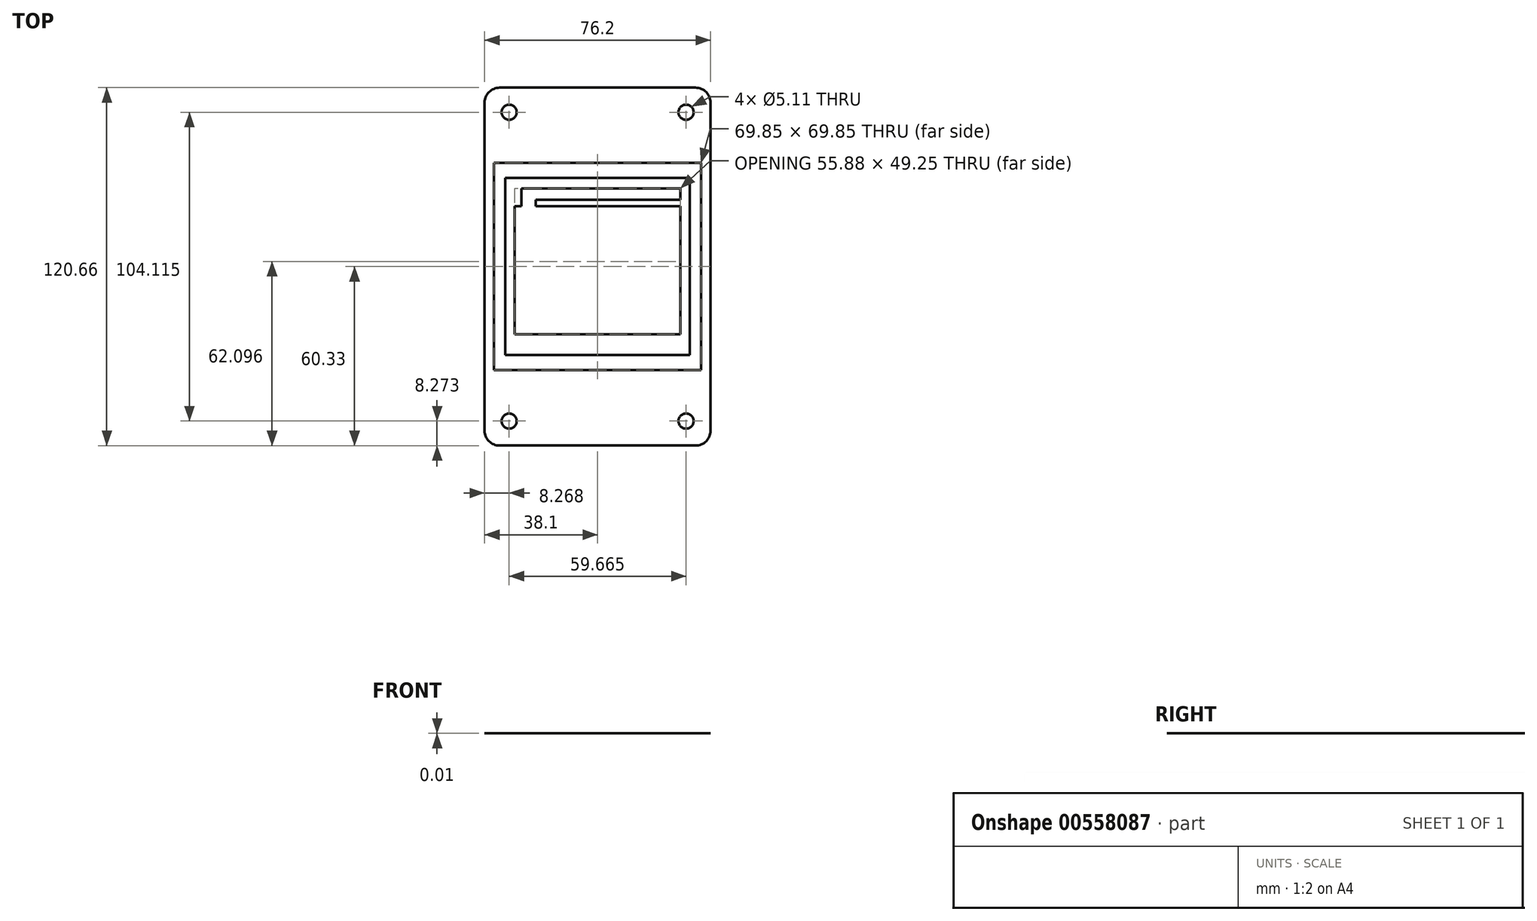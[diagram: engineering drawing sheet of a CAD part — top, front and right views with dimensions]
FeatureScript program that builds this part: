
annotation { "Feature Type Name" : "Feature", "Feature Type Description" : "" }
export const myFeature = defineFeature(function(context is Context, id is Id, definition is map)
    precondition{}
    {
        {
            var Q0;
            Q0=qCreatedBy(makeId("Top.planeOp"),FACE);
            var sketch = newSketch(context, id + "F0", { "sketchPlane" : qUnion([Q0])});
            skLineSegment(sketch, "E0.bottom", {"start": v(-38.1, 60.33) * mm, "end": v(38.1, 60.33) * mm});
            skLineSegment(sketch, "E0.top", {"start": v(-38.1, -60.33) * mm, "end": v(38.1, -60.32) * mm});
            skLineSegment(sketch, "E0.left", {"start": v(-38.1, 60.33) * mm, "end": v(-38.1, -60.33) * mm});
            skLineSegment(sketch, "E0.right", {"start": v(38.1, 60.33) * mm, "end": v(38.1, -60.32) * mm});
            skCircle(sketch, "E1", {"center": v(-29.83, 52.06) * mm, "radius": 2.55 * mm});
            skCircle(sketch, "E2", {"center": v(-29.83, -52.06) * mm, "radius": 2.55 * mm});
            skCircle(sketch, "E3", {"center": v(29.83, -52.06) * mm, "radius": 2.55 * mm});
            skLineSegment(sketch, "E4.bottom", {"start": v(-29.83, 52.06) * mm, "end": v(29.83, 52.06) * mm, "construction": true});
            skLineSegment(sketch, "E4.top", {"start": v(-29.83, -52.06) * mm, "end": v(29.83, -52.06) * mm, "construction": true});
            skLineSegment(sketch, "E4.left", {"start": v(-29.83, 52.06) * mm, "end": v(-29.83, -52.06) * mm, "construction": true});
            skLineSegment(sketch, "E4.right", {"start": v(29.83, 52.06) * mm, "end": v(29.83, -52.06) * mm, "construction": true});
            skPoint(sketch, "E4.middle", {"position": v(0, 0) * mm});
            skCircle(sketch, "E5", {"center": v(29.83, 52.06) * mm, "radius": 2.55 * mm});
            skSolve(sketch);
        }
        {
            var Q0;
            Q0=makeQuery(id+"F0.imprint","IMPRINT",FACE,{"disambiguationData":[TD([[makeQuery(id+"F0.imprint","IMPRINT",EDGE,{"derivedFrom":sQuery(id+"F0.wireOp",EDGE,"E0.bottom")}),-1.0]])]});
            extrude(context, id + "F1", {"entities" : qUnion([Q0]), "depth" : 1 / 101.6 * mm, "offsetDistance" : 25.4 * mm});
        }
        {
            var Q0;
            Q0=makeQuery(id+"F1.opExtrude","CAP_FACE",FACE,{"disambiguationData":[OSD([sQuery(id+"F0.wireOp",EDGE,"E0.bottom"),sQuery(id+"F0.wireOp",EDGE,"E0.top"),sQuery(id+"F0.wireOp",EDGE,"E0.left"),sQuery(id+"F0.wireOp",EDGE,"E0.right"),sQuery(id+"F0.wireOp",EDGE,"E1"),sQuery(id+"F0.wireOp",EDGE,"d460dd98-078a-4822-9f90-65cb2c6fe7cf"),sQuery(id+"F0.wireOp",EDGE,"E2"),sQuery(id+"F0.wireOp",EDGE,"E3")])],"isStart":false});
            var sketch = newSketch(context, id + "F2", { "sketchPlane" : qUnion([Q0])});
            skCircle(sketch, "E6", {"center": v(0, 0) * mm, "radius": 9.53 * mm});
            skLineSegment(sketch, "E7.bottom", {"start": v(-27.94, 20.32) * mm, "end": v(27.94, 20.32) * mm});
            skLineSegment(sketch, "E7.top", {"start": v(-27.94, -22.86) * mm, "end": v(27.94, -22.86) * mm});
            skLineSegment(sketch, "E7.left", {"start": v(-27.94, 20.32) * mm, "end": v(-27.94, -22.86) * mm});
            skLineSegment(sketch, "E7.right", {"start": v(27.94, 20.32) * mm, "end": v(27.94, -22.86) * mm});
            skSolve(sketch);
        }
        {
            var Q0;
            Q0=makeQuery(id+"F2.imprint","IMPRINT",FACE,{"disambiguationData":[TD([[makeQuery(id+"F2.imprint","IMPRINT",EDGE,{"derivedFrom":sQuery(id+"F2.wireOp",EDGE,"E6")}),1.0]])]});
            extrude(context, id + "F3", {"entities" : qUnion([Q0]), "operationType" : NewBodyOperationType.REMOVE, "oppositeDirection" : true, "depth" : 1 / 101.6 * mm, "offsetDistance" : 25.4 * mm});
        }
        {
            var Q0;
            Q0=makeQuery(id+"F2.imprint","IMPRINT",FACE,{"disambiguationData":[TD([[makeQuery(id+"F2.imprint","IMPRINT",EDGE,{"derivedFrom":sQuery(id+"F2.wireOp",EDGE,"E6")}),-1.0]])]});
            extrude(context, id + "F4", {"entities" : qUnion([Q0]), "operationType" : NewBodyOperationType.REMOVE, "oppositeDirection" : true, "depth" : 5 * mm, "offsetDistance" : 25.4 * mm});
        }
        {
            var Q0;
            Q0=makeQuery(id+"F1.opExtrude","SWEPT_EDGE",EDGE,{"disambiguationData":[OSD([sQuery(id+"F0.wireOp",EDGE,"E0.top"),sQuery(id+"F0.wireOp",EDGE,"E0.right")])]});
            var Q1;
            Q1=makeQuery(id+"F1.opExtrude","SWEPT_EDGE",EDGE,{"disambiguationData":[OSD([sQuery(id+"F0.wireOp",EDGE,"E0.bottom"),sQuery(id+"F0.wireOp",EDGE,"E0.right")])]});
            var Q2;
            Q2=makeQuery(id+"F1.opExtrude","SWEPT_EDGE",EDGE,{"disambiguationData":[OSD([sQuery(id+"F0.wireOp",EDGE,"E0.bottom"),sQuery(id+"F0.wireOp",EDGE,"E0.left")])]});
            var Q3;
            Q3=makeQuery(id+"F1.opExtrude","SWEPT_EDGE",EDGE,{"disambiguationData":[OSD([sQuery(id+"F0.wireOp",EDGE,"E0.top"),sQuery(id+"F0.wireOp",EDGE,"E0.left")])]});
            fillet(context, id + "F5", {"entities" : qUnion([Q0, Q1, Q2, Q3]), "radius" : 5.08 * mm, "tangentPropagation" : true, "allowEdgeOverflow" : false});
        }
        {
            var Q0;
            Q0=makeQuery(id+"F1.opExtrude","CAP_FACE",FACE,{"disambiguationData":[OSD([sQuery(id+"F0.wireOp",EDGE,"E0.bottom"),sQuery(id+"F0.wireOp",EDGE,"E0.top"),sQuery(id+"F0.wireOp",EDGE,"E0.left"),sQuery(id+"F0.wireOp",EDGE,"E0.right"),sQuery(id+"F0.wireOp",EDGE,"E1"),sQuery(id+"F0.wireOp",EDGE,"d460dd98-078a-4822-9f90-65cb2c6fe7cf"),sQuery(id+"F0.wireOp",EDGE,"E2"),sQuery(id+"F0.wireOp",EDGE,"E3")])],"isStart":false});
            var sketch = newSketch(context, id + "F6", { "sketchPlane" : qUnion([Q0])});
            skLineSegment(sketch, "E8.bottom", {"start": v(34.93, -34.92) * mm, "end": v(-34.93, -34.93) * mm});
            skLineSegment(sketch, "E8.top", {"start": v(34.92, 34.93) * mm, "end": v(-34.93, 34.92) * mm});
            skLineSegment(sketch, "E8.left", {"start": v(34.93, -34.92) * mm, "end": v(34.92, 34.93) * mm});
            skLineSegment(sketch, "E8.right", {"start": v(-34.93, -34.93) * mm, "end": v(-34.93, 34.92) * mm});
            skLineSegment(sketch, "E9.bottom", {"start": v(31.12, -29.85) * mm, "end": v(-31.12, -29.85) * mm});
            skLineSegment(sketch, "E9.top", {"start": v(31.12, 29.85) * mm, "end": v(-31.12, 29.85) * mm});
            skLineSegment(sketch, "E9.left", {"start": v(31.12, -29.85) * mm, "end": v(31.12, 29.85) * mm});
            skLineSegment(sketch, "E9.right", {"start": v(-31.12, -29.85) * mm, "end": v(-31.12, 29.85) * mm});
            skSolve(sketch);
        }
        {
            var Q0;
            Q0=makeQuery(id+"F6.imprint","IMPRINT",FACE,{"disambiguationData":[TD([[makeQuery(id+"F6.imprint","IMPRINT",EDGE,{"derivedFrom":sQuery(id+"F6.wireOp",EDGE,"E8.bottom")}),-1.0]])]});
            extrude(context, id + "F7", {"entities" : qUnion([Q0]), "operationType" : NewBodyOperationType.REMOVE, "oppositeDirection" : true, "depth" : 0.06 * 17.78 * mm, "offsetDistance" : 25.4 * mm});
        }
        {
            var Q0;
            Q0=makeQuery(id+"F7.boolean.opBoolean","SPLIT",FACE,{"disambiguationData":[TD([makeQuery(id+"F4.boolean.opBoolean","COPY",FACE,{"derivedFrom":makeQuery(id+"F4.opExtrude","SWEPT_FACE",FACE,{"disambiguationData":[OSD([sQuery(id+"F2.wireOp",EDGE,"E7.bottom")])]})})])],"derivedFrom":makeQuery(id+"F1.opExtrude","CAP_FACE",FACE,{"disambiguationData":[OSD([sQuery(id+"F0.wireOp",EDGE,"E0.bottom"),sQuery(id+"F0.wireOp",EDGE,"E0.top"),sQuery(id+"F0.wireOp",EDGE,"E0.left"),sQuery(id+"F0.wireOp",EDGE,"E0.right"),sQuery(id+"F0.wireOp",EDGE,"E1"),sQuery(id+"F0.wireOp",EDGE,"d460dd98-078a-4822-9f90-65cb2c6fe7cf"),sQuery(id+"F0.wireOp",EDGE,"E2"),sQuery(id+"F0.wireOp",EDGE,"E3")])],"isStart":false})});
            var sketch = newSketch(context, id + "F8", { "sketchPlane" : qUnion([Q0])});
            skLineSegment(sketch, "E10", {"start": v(-20.9, 20.32) * mm, "end": v(-20.9, 22.5) * mm});
            skLineSegment(sketch, "E11", {"start": v(-20.9, 22.5) * mm, "end": v(27.94, 22.5) * mm});
            skLineSegment(sketch, "E12", {"start": v(27.94, 22.5) * mm, "end": v(27.94, 26.4) * mm});
            skLineSegment(sketch, "E13", {"start": v(27.94, 26.4) * mm, "end": v(-25.7, 26.4) * mm});
            skLineSegment(sketch, "E14", {"start": v(-25.7, 26.4) * mm, "end": v(-25.7, 20.32) * mm});
            skSolve(sketch);
        }
        {
            var Q0;
            {var subQ0=sQuery(id+"F8.wireOp",EDGE,"E10");Q0=makeQuery(id+"F8.imprint","IMPRINT",FACE,{"disambiguationData":[TD([[makeQuery(id+"F8.imprint","IMPRINT",EDGE,{"derivedFrom":subQ0}),1.0]])]});}
            extrude(context, id + "F9", {"entities" : qUnion([Q0]), "operationType" : NewBodyOperationType.REMOVE, "oppositeDirection" : true, "depth" : 5 * mm, "offsetDistance" : 25.4 * mm});
        }
    });
